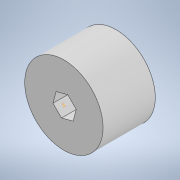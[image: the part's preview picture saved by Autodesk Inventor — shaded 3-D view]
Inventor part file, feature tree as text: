
AUTODESK INVENTOR PART (.ipt)
format: ipt  version: 2021.2 (Build 252289000, 289)  size: 136,192 bytes
history: native  units: mm
features: sketch x4, other x2, extrude x2
ambient origin geometry x8: Origin, YZ Plane, XZ Plane, XY Plane, X Axis, Y Axis, Z Axis, Center Point
bodies: Body1 (feature_tree)
feature tree (8):
  other  "Твердое тело1"
  extrude  "Выдавливание1"  Depth=15.0mm
  extrude  "Выдавливание2"  Depth=10.0mm TaperAngle=0.0deg
  sketch  "Эскиз3"
  other  "Параметрическийэлемент1:1"
  sketch  "Эскиз1"
  sketch  "Эскиз2"
  sketch  "Эскиз4"
